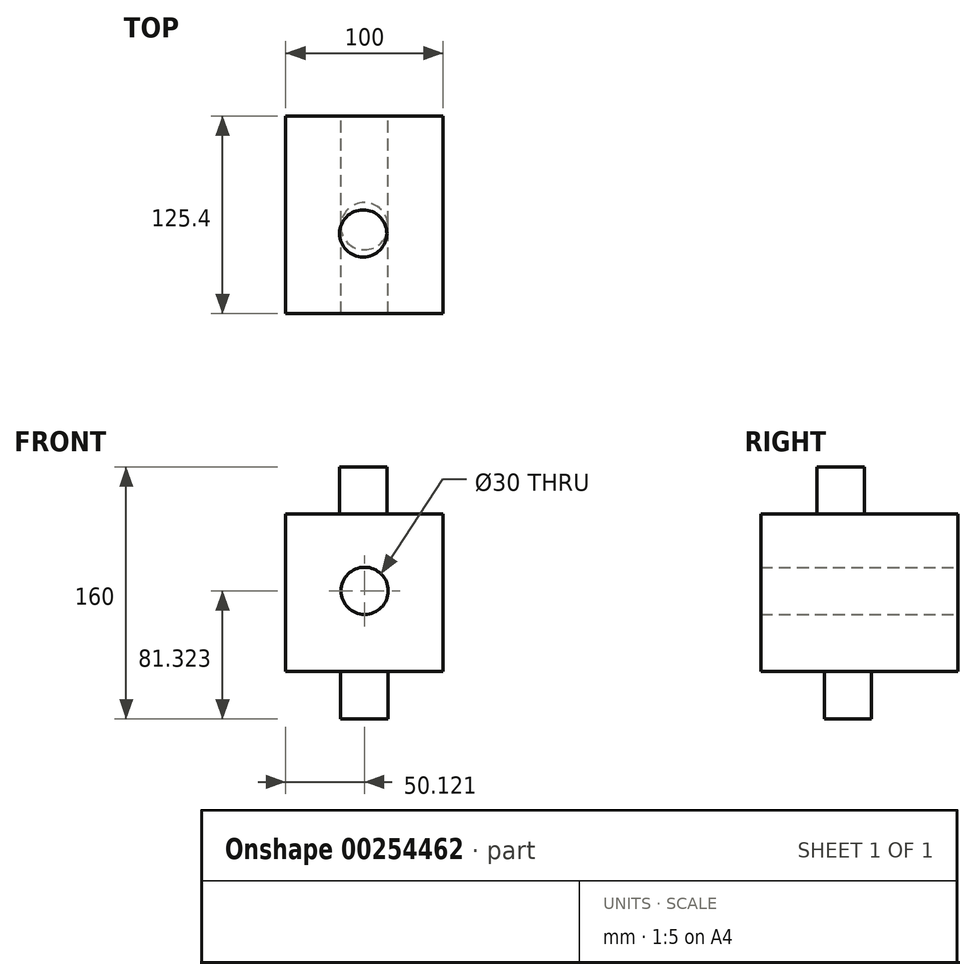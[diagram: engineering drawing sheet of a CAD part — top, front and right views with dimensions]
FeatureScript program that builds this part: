
annotation { "Feature Type Name" : "Feature", "Feature Type Description" : "" }
export const myFeature = defineFeature(function(context is Context, id is Id, definition is map)
    precondition{}
    {
        {
            var Q0;
            Q0=qCreatedBy(makeId("Front.planeOp"),FACE);
            var sketch = newSketch(context, id + "F0", { "sketchPlane" : qUnion([Q0])});
            skLineSegment(sketch, "E0.bottom", {"start": v(0, 0) * mm, "end": v(100, 0) * mm});
            skLineSegment(sketch, "E0.top", {"start": v(0, 100) * mm, "end": v(100, 100) * mm});
            skLineSegment(sketch, "E0.left", {"start": v(0, 0) * mm, "end": v(0, 100) * mm});
            skLineSegment(sketch, "E0.right", {"start": v(100, 0) * mm, "end": v(100, 100) * mm});
            skSolve(sketch);
        }
        {
            var Q0;
            Q0=makeQuery(id+"F0.imprint","IMPRINT",FACE,{"disambiguationData":[TD([[makeQuery(id+"F0.imprint","IMPRINT",EDGE,{"derivedFrom":sQuery(id+"F0.wireOp",EDGE,"E0.bottom")}),1.0]])]});
            extrude(context, id + "F1", {"entities" : qUnion([Q0]), "depth" : 100 * mm});
        }
        {
            var Q0;
            Q0=makeQuery(id+"F1.opExtrude","SWEPT_FACE",FACE,{"disambiguationData":[OSD([sQuery(id+"F0.wireOp",EDGE,"E0.top")])]});
            var sketch = newSketch(context, id + "F2", { "sketchPlane" : qUnion([Q0])});
            skPoint(sketch, "E1", {"position": v(49.25, -49.22) * mm});
            skCircle(sketch, "E2", {"center": v(49.25, -49.22) * mm, "radius": 15 * mm});
            skSolve(sketch);
        }
        {
            var Q0;
            Q0=makeQuery(id+"F1.opExtrude","SWEPT_FACE",FACE,{"disambiguationData":[OSD([sQuery(id+"F0.wireOp",EDGE,"E0.bottom")])]});
            var sketch = newSketch(context, id + "F3", { "sketchPlane" : qUnion([Q0])});
            skPoint(sketch, "E3", {"position": v(50, 44.53) * mm});
            skCircle(sketch, "E4", {"center": v(50, 44.53) * mm, "radius": 15 * mm});
            skSolve(sketch);
        }
        {
            var Q0;
            Q0 = qSketchRegion(id + "F3", true);
            extrude(context, id + "F4", {"entities" : qUnion([Q0]), "operationType" : NewBodyOperationType.ADD, "depth" : 30 * mm});
        }
        {
            var Q0;
            Q0=makeQuery(id+"F2.imprint","IMPRINT",FACE,{"disambiguationData":[TD([[makeQuery(id+"F2.imprint","IMPRINT",EDGE,{"derivedFrom":sQuery(id+"F2.wireOp",EDGE,"E2")}),1.0]])]});
            extrude(context, id + "F5", {"entities" : qUnion([Q0]), "operationType" : NewBodyOperationType.ADD, "depth" : 30 * mm});
        }
        {
            var Q0;
            Q0=makeQuery(id+"F1.opExtrude","CAP_FACE",FACE,{"disambiguationData":[OSD([sQuery(id+"F0.wireOp",EDGE,"E0.bottom"),sQuery(id+"F0.wireOp",EDGE,"E0.top"),sQuery(id+"F0.wireOp",EDGE,"E0.left"),sQuery(id+"F0.wireOp",EDGE,"E0.right")])],"isStart":true});
            var sketch = newSketch(context, id + "F6", { "sketchPlane" : qUnion([Q0])});
            skSolve(sketch);
        }
        {
            var Q0;
            Q0=makeQuery(id+"F6.imprint","IMPRINT",FACE,{"disambiguationData":[TD([[makeQuery(id+"F6.imprint","IMPRINT",EDGE,{"derivedFrom":makeQuery(id+"F1.opExtrude","CAP_EDGE",EDGE,{"disambiguationData":[OSD([sQuery(id+"F0.wireOp",EDGE,"E0.bottom")])],"isStart":true})}),-1.0]])]});
            extrude(context, id + "F7", {"entities" : qUnion([Q0]), "operationType" : NewBodyOperationType.ADD, "depth" : 25.4 * mm});
        }
        {
            var Q0;
            Q0=makeQuery(id+"F7.opExtrude","CAP_FACE",FACE,{"disambiguationData":[OSD([sQuery(id+"F0.wireOp",EDGE,"E0.bottom"),sQuery(id+"F0.wireOp",EDGE,"E0.top"),sQuery(id+"F0.wireOp",EDGE,"E0.left"),sQuery(id+"F0.wireOp",EDGE,"E0.right")])],"isStart":false});
            var sketch = newSketch(context, id + "F8", { "sketchPlane" : qUnion([Q0])});
            skPoint(sketch, "E5", {"position": v(-50.12, 51.32) * mm});
            skSolve(sketch);
        }
        {
            var Q0;
            Q0=sQuery(id+"F8.wireOp",VERTEX,"E5");
            var Q1;
            Q1=makeQuery(id+"F1.opExtrude","SWEPT_BODY",BODY,{"disambiguationData":[OSD([sQuery(id+"F0.wireOp",EDGE,"E0.bottom"),sQuery(id+"F0.wireOp",EDGE,"E0.top"),sQuery(id+"F0.wireOp",EDGE,"E0.left"),sQuery(id+"F0.wireOp",EDGE,"E0.right")])]});
            hole(context, id + "F9", {"style" : HoleStyle.SIMPLE, "endStyle" : HoleEndStyle.THROUGH, "holeDiameter" : 30 * mm, "tappedDepth" : 12.7 * mm, "tapClearance" : 3, "locations" : qUnion([Q0]), "scope" : qUnion([Q1])});
        }
    });
